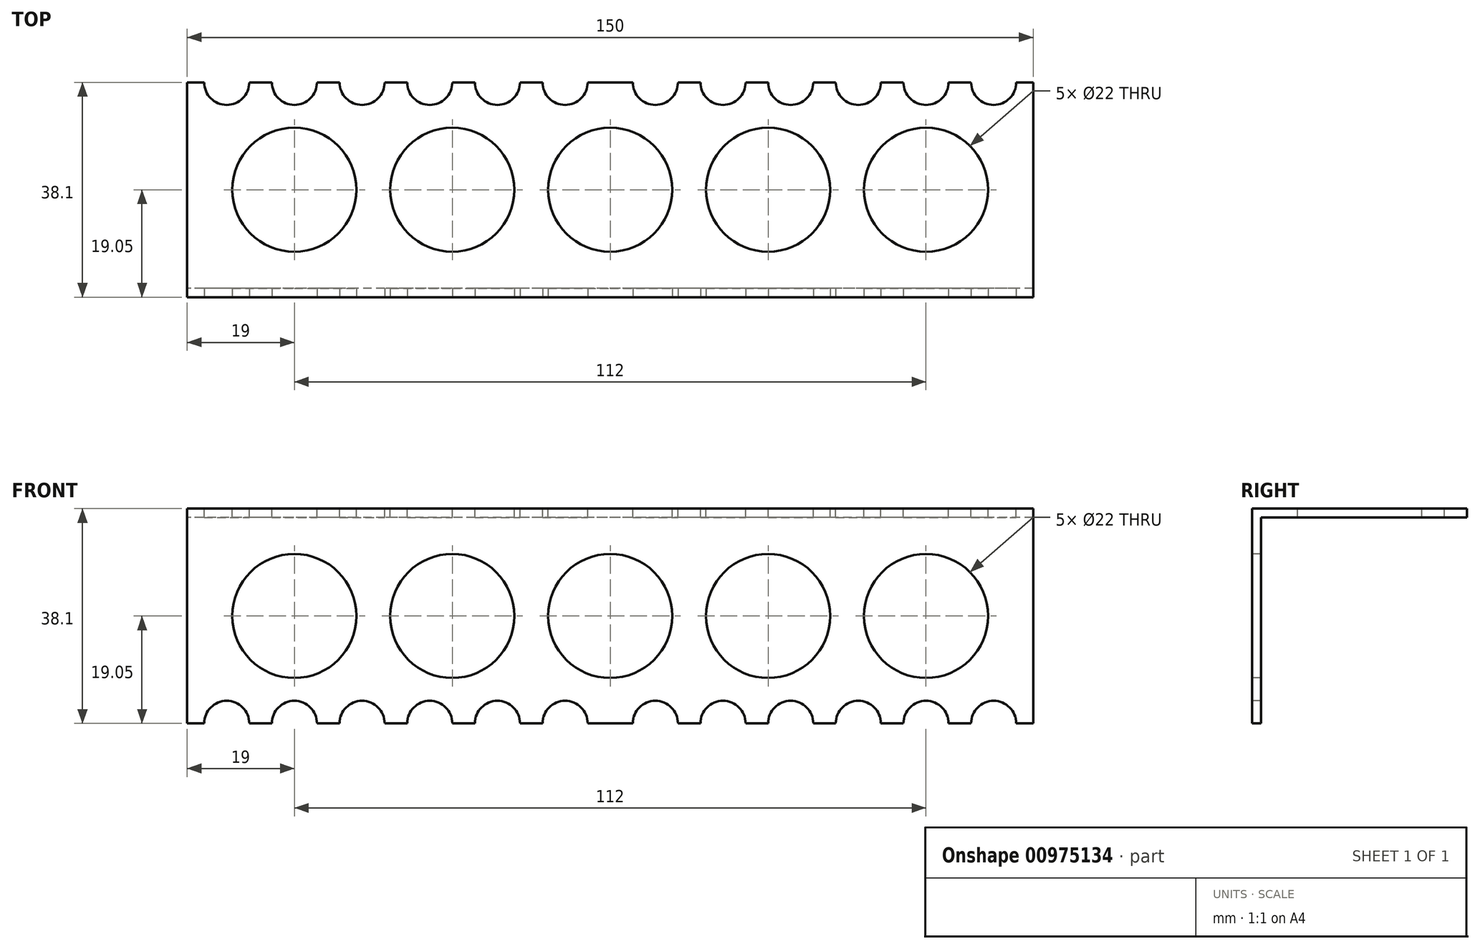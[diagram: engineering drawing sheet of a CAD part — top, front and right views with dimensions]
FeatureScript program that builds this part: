
annotation { "Feature Type Name" : "Feature", "Feature Type Description" : "" }
export const myFeature = defineFeature(function(context is Context, id is Id, definition is map)
    precondition{}
    {
        {
            var Q0;
            Q0=qCreatedBy(makeId("Right.planeOp"),FACE);
            var sketch = newSketch(context, id + "F0", { "sketchPlane" : qUnion([Q0])});
            skLineSegment(sketch, "E0.bottom", {"start": v(0, 0) * mm, "end": v(1.59, 0) * mm});
            skLineSegment(sketch, "E0.left", {"start": v(0, 0) * mm, "end": v(0, 38.1) * mm});
            skLineSegment(sketch, "E0.right", {"start": v(1.59, 0) * mm, "end": v(1.59, 36.51) * mm});
            skLineSegment(sketch, "E1.bottom", {"start": v(0, 38.1) * mm, "end": v(38.1, 38.1) * mm});
            skLineSegment(sketch, "E1.top", {"start": v(1.59, 36.51) * mm, "end": v(38.1, 36.51) * mm});
            skLineSegment(sketch, "E1.right", {"start": v(38.1, 38.1) * mm, "end": v(38.1, 36.51) * mm});
            skSolve(sketch);
        }
        {
            var Q0;
            Q0 = qSketchRegion(id + "F0", true);
            extrude(context, id + "F1", {"entities" : qUnion([Q0]), "depth" : 150 * mm, "offsetDistance" : 25 * mm});
        }
        {
            var Q0;
            Q0=makeQuery(id+"F1.opExtrude","SWEPT_FACE",FACE,{"disambiguationData":[OSD([sQuery(id+"F0.wireOp",EDGE,"E0.left")])]});
            var sketch = newSketch(context, id + "F2", { "sketchPlane" : qUnion([Q0])});
            skCircle(sketch, "E2", {"center": v(75, 19.05) * mm, "radius": 11 * mm});
            skLineSegment(sketch, "E3", {"start": v(0, 19.05) * mm, "end": v(150, 19.05) * mm, "construction": true});
            skLineSegment(sketch, "E4", {"start": v(75, 38.1) * mm, "end": v(75, 0) * mm, "construction": true});
            skLineSegment(sketch, "E5", {"start": v(103, 38.1) * mm, "end": v(103, 0) * mm, "construction": true});
            skLineSegment(sketch, "E6", {"start": v(131, 38.1) * mm, "end": v(131, 0) * mm, "construction": true});
            skCircle(sketch, "E7", {"center": v(103, 19.05) * mm, "radius": 11 * mm});
            skCircle(sketch, "E8", {"center": v(131, 19.05) * mm, "radius": 11 * mm});
            skCircle(sketch, "E9.MirrorC", {"center": v(47, 19.05) * mm, "radius": 11 * mm});
            skCircle(sketch, "E10.MirrorC", {"center": v(19, 19.05) * mm, "radius": 11 * mm});
            skArc(sketch, "E11", {"start": v(79, 0) * mm, "mid": v(83, 4) * mm, "end": v(87, 0) * mm});
            skLineSegment(sketch, "E12", {"start": v(87, 0) * mm, "end": v(79, 0) * mm});
            skLineSegment(sketch, "E13.1.0.0", {"start": v(99, 0) * mm, "end": v(91, 0) * mm});
            skArc(sketch, "E13.1.0.1", {"start": v(91, 0) * mm, "mid": v(95, 4) * mm, "end": v(99, 0) * mm});
            skLineSegment(sketch, "E13.2.0.0", {"start": v(111, 0) * mm, "end": v(103, 0) * mm});
            skArc(sketch, "E13.2.0.1", {"start": v(103, 0) * mm, "mid": v(107, 4) * mm, "end": v(111, 0) * mm});
            skLineSegment(sketch, "E13.3.0.0", {"start": v(123, 0) * mm, "end": v(115, 0) * mm});
            skArc(sketch, "E13.3.0.1", {"start": v(115, 0) * mm, "mid": v(119, 4) * mm, "end": v(123, 0) * mm});
            skLineSegment(sketch, "E13.4.0.0", {"start": v(135, 0) * mm, "end": v(127, 0) * mm});
            skArc(sketch, "E13.4.0.1", {"start": v(127, 0) * mm, "mid": v(131, 4) * mm, "end": v(135, 0) * mm});
            skLineSegment(sketch, "E13.5.0.0", {"start": v(147, 0) * mm, "end": v(139, 0) * mm});
            skArc(sketch, "E13.5.0.1", {"start": v(139, 0) * mm, "mid": v(143, 4) * mm, "end": v(147, 0) * mm});
            skLineSegment(sketch, "E13.direction1", {"start": v(79, 0) * mm, "end": v(91, 0) * mm, "construction": true});
            skLineSegment(sketch, "E14.MirrorCS", {"start": v(63, 0) * mm, "end": v(71, 0) * mm});
            skLineSegment(sketch, "E15.MirrorCS", {"start": v(3, 0) * mm, "end": v(11, 0) * mm});
            skLineSegment(sketch, "E16.MirrorCS", {"start": v(27, 0) * mm, "end": v(35, 0) * mm});
            skArc(sketch, "E17.MirrorCS", {"start": v(11, 0) * mm, "mid": v(7, 4) * mm, "end": v(3, 0) * mm});
            skArc(sketch, "E18.MirrorCS", {"start": v(35, 0) * mm, "mid": v(31, 4) * mm, "end": v(27, 0) * mm});
            skLineSegment(sketch, "E19.MirrorCS", {"start": v(15, 0) * mm, "end": v(23, 0) * mm});
            skArc(sketch, "E20.MirrorCS", {"start": v(47, 0) * mm, "mid": v(43, 4) * mm, "end": v(39, 0) * mm});
            skArc(sketch, "E21.MirrorCS", {"start": v(71, 0) * mm, "mid": v(67, 4) * mm, "end": v(63, 0) * mm});
            skArc(sketch, "E22.MirrorCS", {"start": v(59, 0) * mm, "mid": v(55, 4) * mm, "end": v(51, 0) * mm});
            skArc(sketch, "E23.MirrorCS", {"start": v(23, 0) * mm, "mid": v(19, 4) * mm, "end": v(15, 0) * mm});
            skLineSegment(sketch, "E24.MirrorCS", {"start": v(71, 0) * mm, "end": v(59, 0) * mm, "construction": true});
            skLineSegment(sketch, "E25.MirrorCS", {"start": v(39, 0) * mm, "end": v(47, 0) * mm});
            skLineSegment(sketch, "E26.MirrorCS", {"start": v(51, 0) * mm, "end": v(59, 0) * mm});
            skSolve(sketch);
        }
        {
            var Q0;
            Q0 = qSketchRegion(id + "F2", true);
            extrude(context, id + "F3", {"entities" : qUnion([Q0]), "operationType" : NewBodyOperationType.REMOVE, "endBound" : BoundingType.THROUGH_ALL, "oppositeDirection" : true, "depth" : 25 * mm, "offsetDistance" : 25 * mm});
        }
        {
            var Q0;
            Q0=makeQuery(id+"F1.opExtrude","SWEPT_FACE",FACE,{"disambiguationData":[OSD([sQuery(id+"F0.wireOp",EDGE,"E1.bottom")])]});
            var sketch = newSketch(context, id + "F4", { "sketchPlane" : qUnion([Q0])});
            skCircle(sketch, "E27", {"center": v(75, 19.05) * mm, "radius": 11 * mm});
            skLineSegment(sketch, "E28", {"start": v(151.2, 19.05) * mm, "end": v(-1.2, 19.05) * mm, "construction": true});
            skLineSegment(sketch, "E29", {"start": v(75, 0) * mm, "end": v(75, 38.1) * mm, "construction": true});
            skLineSegment(sketch, "E30", {"start": v(47, 0) * mm, "end": v(47, 38.1) * mm, "construction": true});
            skLineSegment(sketch, "E31", {"start": v(19, 0) * mm, "end": v(19, 38.1) * mm, "construction": true});
            skCircle(sketch, "E32", {"center": v(47, 19.05) * mm, "radius": 11 * mm});
            skCircle(sketch, "E33", {"center": v(19, 19.05) * mm, "radius": 11 * mm});
            skCircle(sketch, "E34.MirrorC", {"center": v(103, 19.05) * mm, "radius": 11 * mm});
            skCircle(sketch, "E35.MirrorC", {"center": v(131, 19.05) * mm, "radius": 11 * mm});
            skArc(sketch, "E36", {"start": v(69.1, 41.5) * mm, "mid": v(67, 34.1) * mm, "end": v(64.9, 41.5) * mm});
            skLineSegment(sketch, "E37", {"start": v(64.9, 41.5) * mm, "end": v(69.1, 41.5) * mm});
            skLineSegment(sketch, "E38.1.0.0", {"start": v(52.9, 41.5) * mm, "end": v(57.1, 41.5) * mm});
            skArc(sketch, "E38.1.0.1", {"start": v(57.1, 41.5) * mm, "mid": v(55, 34.1) * mm, "end": v(52.9, 41.5) * mm});
            skLineSegment(sketch, "E38.2.0.0", {"start": v(40.9, 41.5) * mm, "end": v(45.1, 41.5) * mm});
            skArc(sketch, "E38.2.0.1", {"start": v(45.1, 41.5) * mm, "mid": v(43, 34.1) * mm, "end": v(40.9, 41.5) * mm});
            skLineSegment(sketch, "E38.3.0.0", {"start": v(28.9, 41.5) * mm, "end": v(33.1, 41.5) * mm});
            skArc(sketch, "E38.3.0.1", {"start": v(33.1, 41.5) * mm, "mid": v(31, 34.1) * mm, "end": v(28.9, 41.5) * mm});
            skLineSegment(sketch, "E38.4.0.0", {"start": v(16.9, 41.5) * mm, "end": v(21.1, 41.5) * mm});
            skArc(sketch, "E38.4.0.1", {"start": v(21.1, 41.5) * mm, "mid": v(19, 34.1) * mm, "end": v(16.9, 41.5) * mm});
            skLineSegment(sketch, "E38.5.0.0", {"start": v(4.9, 41.5) * mm, "end": v(9.1, 41.5) * mm});
            skArc(sketch, "E38.5.0.1", {"start": v(9.1, 41.5) * mm, "mid": v(7, 34.1) * mm, "end": v(4.9, 41.5) * mm});
            skLineSegment(sketch, "E38.direction1", {"start": v(69.1, 41.5) * mm, "end": v(57.1, 41.5) * mm, "construction": true});
            skLineSegment(sketch, "E39.MirrorCS", {"start": v(85.1, 41.5) * mm, "end": v(80.9, 41.5) * mm});
            skLineSegment(sketch, "E40.MirrorCS", {"start": v(145.1, 41.5) * mm, "end": v(140.9, 41.5) * mm});
            skLineSegment(sketch, "E41.MirrorCS", {"start": v(121.1, 41.5) * mm, "end": v(116.9, 41.5) * mm});
            skArc(sketch, "E42.MirrorCS", {"start": v(140.9, 41.5) * mm, "mid": v(143, 34.1) * mm, "end": v(145.1, 41.5) * mm});
            skArc(sketch, "E43.MirrorCS", {"start": v(116.9, 41.5) * mm, "mid": v(119, 34.1) * mm, "end": v(121.1, 41.5) * mm});
            skLineSegment(sketch, "E44.MirrorCS", {"start": v(133.1, 41.5) * mm, "end": v(128.9, 41.5) * mm});
            skArc(sketch, "E45.MirrorCS", {"start": v(104.9, 41.5) * mm, "mid": v(107, 34.1) * mm, "end": v(109.1, 41.5) * mm});
            skArc(sketch, "E46.MirrorCS", {"start": v(80.9, 41.5) * mm, "mid": v(83, 34.1) * mm, "end": v(85.1, 41.5) * mm});
            skArc(sketch, "E47.MirrorCS", {"start": v(92.9, 41.5) * mm, "mid": v(95, 34.1) * mm, "end": v(97.1, 41.5) * mm});
            skArc(sketch, "E48.MirrorCS", {"start": v(128.9, 41.5) * mm, "mid": v(131, 34.1) * mm, "end": v(133.1, 41.5) * mm});
            skLineSegment(sketch, "E49.MirrorCS", {"start": v(80.9, 41.5) * mm, "end": v(92.9, 41.5) * mm, "construction": true});
            skLineSegment(sketch, "E50.MirrorCS", {"start": v(109.1, 41.5) * mm, "end": v(104.9, 41.5) * mm});
            skLineSegment(sketch, "E51.MirrorCS", {"start": v(97.1, 41.5) * mm, "end": v(92.9, 41.5) * mm});
            skSolve(sketch);
        }
        {
            var Q0;
            Q0 = qSketchRegion(id + "F4", true);
            extrude(context, id + "F5", {"entities" : qUnion([Q0]), "operationType" : NewBodyOperationType.REMOVE, "endBound" : BoundingType.THROUGH_ALL, "oppositeDirection" : true, "depth" : 25 * mm, "offsetDistance" : 25 * mm});
        }
    });
